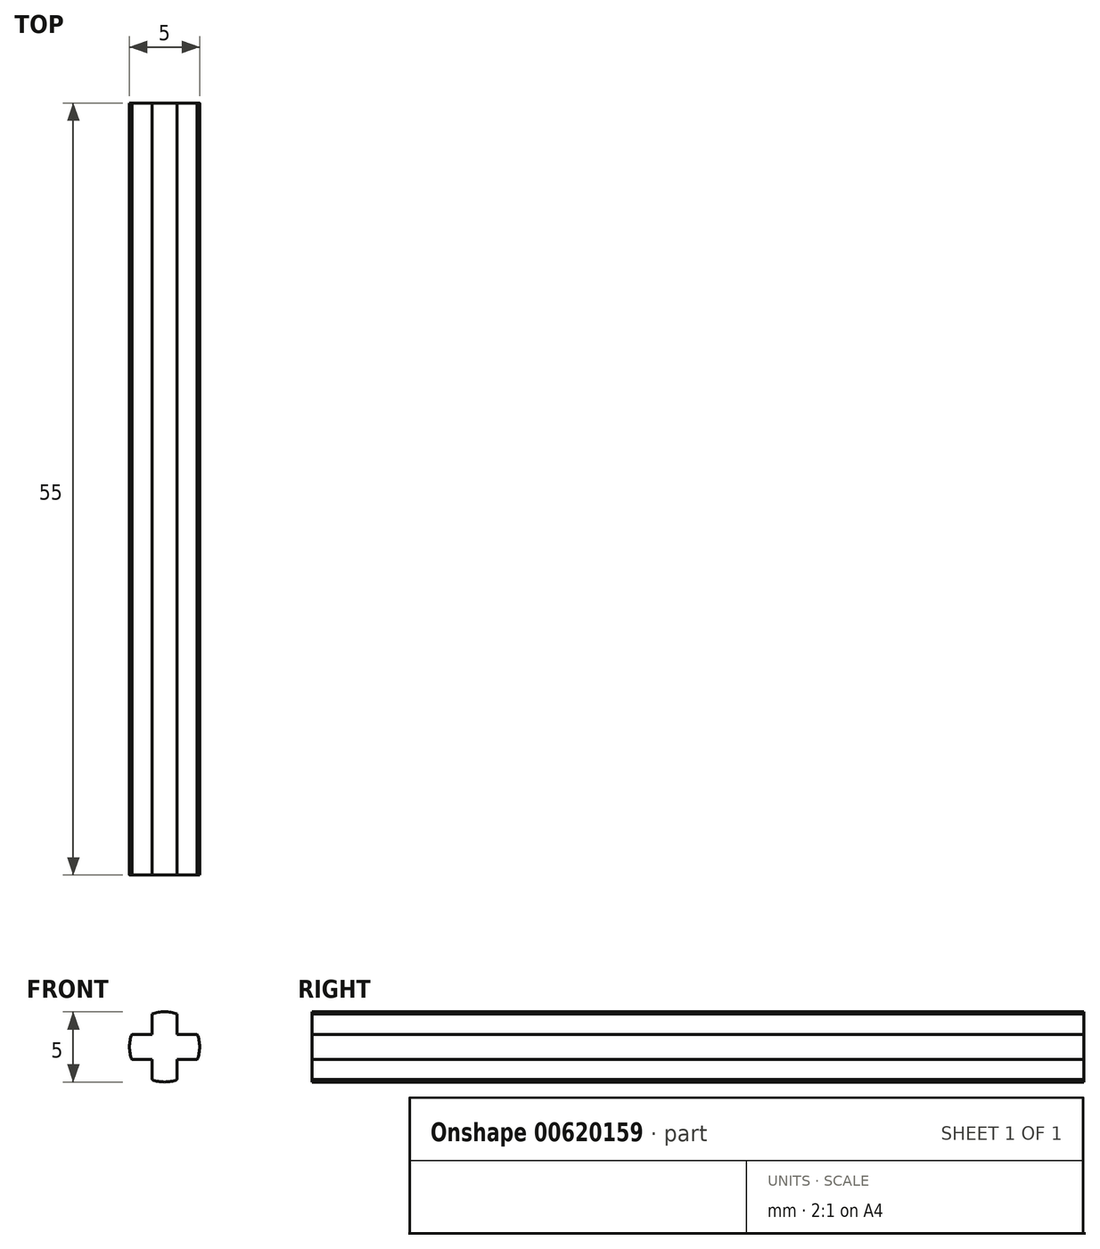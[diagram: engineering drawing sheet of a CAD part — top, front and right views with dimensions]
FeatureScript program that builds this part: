
annotation { "Feature Type Name" : "Feature", "Feature Type Description" : "" }
export const myFeature = defineFeature(function(context is Context, id is Id, definition is map)
    precondition{}
    {
        {
            var Q0;
            Q0=qCreatedBy(makeId("Front.planeOp"),FACE);
            var sketch = newSketch(context, id + "F0", { "sketchPlane" : qUnion([Q0])});
            skArc(sketch, "E0", {"start": v(2.33, -0.9) * mm, "mid": v(2.5, 0) * mm, "end": v(2.33, 0.9) * mm});
            skLineSegment(sketch, "E1.left", {"start": v(-0.9, 2.33) * mm, "end": v(-0.9, 0.9) * mm});
            skLineSegment(sketch, "E1.right", {"start": v(0.9, 2.33) * mm, "end": v(0.9, 0.9) * mm});
            skLineSegment(sketch, "E2.bottom", {"start": v(2.33, 0.9) * mm, "end": v(0.9, 0.9) * mm});
            skLineSegment(sketch, "E2.top", {"start": v(2.33, -0.9) * mm, "end": v(0.9, -0.9) * mm});
            skArc(sketch, "E3.trimOffspring", {"start": v(0.9, 2.33) * mm, "mid": v(0, 2.5) * mm, "end": v(-0.9, 2.33) * mm});
            skArc(sketch, "E4.trimOffspring", {"start": v(-2.33, 0.9) * mm, "mid": v(-2.5, 0) * mm, "end": v(-2.33, -0.9) * mm});
            skArc(sketch, "E5.trimOffspring", {"start": v(-0.9, -2.33) * mm, "mid": v(0, -2.5) * mm, "end": v(0.9, -2.33) * mm});
            skLineSegment(sketch, "E6.trimOffspring", {"start": v(-0.9, -0.9) * mm, "end": v(-0.9, -2.33) * mm});
            skLineSegment(sketch, "E7.trimOffspring", {"start": v(-0.9, 0.9) * mm, "end": v(-2.33, 0.9) * mm});
            skLineSegment(sketch, "E8.trimOffspring", {"start": v(0.9, -0.9) * mm, "end": v(0.9, -2.33) * mm});
            skLineSegment(sketch, "E9.trimOffspring", {"start": v(-0.9, -0.9) * mm, "end": v(-2.33, -0.9) * mm});
            skSolve(sketch);
        }
        {
            var Q0;
            Q0 = qSketchRegion(id + "F0", true);
            extrude(context, id + "F1", {"entities" : qUnion([Q0]), "endBound" : BoundingType.SYMMETRIC, "depth" : 55 * mm, "offsetDistance" : 25 * mm});
        }
    });
